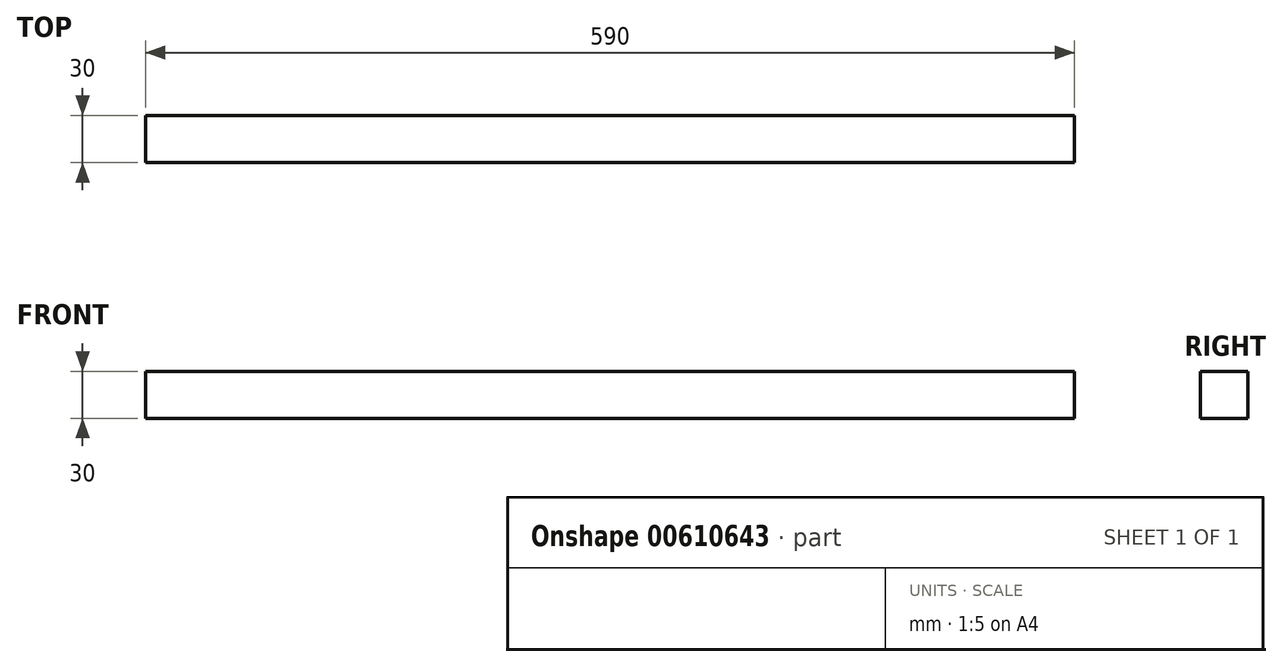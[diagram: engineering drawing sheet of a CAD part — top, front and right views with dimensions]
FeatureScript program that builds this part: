
annotation { "Feature Type Name" : "Feature", "Feature Type Description" : "" }
export const myFeature = defineFeature(function(context is Context, id is Id, definition is map)
    precondition{}
    {
        {
            var Q0;
            Q0=qCreatedBy(makeId("Front.planeOp"),FACE);
            var sketch = newSketch(context, id + "F0", { "sketchPlane" : qUnion([Q0])});
            skLineSegment(sketch, "E0.bottom", {"start": v(-59.04, -188.45) * mm, "end": v(530.96, -188.45) * mm});
            skLineSegment(sketch, "E0.top", {"start": v(-59.04, -218.45) * mm, "end": v(530.96, -218.45) * mm});
            skLineSegment(sketch, "E0.left", {"start": v(-59.04, -188.45) * mm, "end": v(-59.04, -218.45) * mm});
            skLineSegment(sketch, "E0.right", {"start": v(530.96, -188.45) * mm, "end": v(530.96, -218.45) * mm});
            skSolve(sketch);
        }
        {
            var Q0;
            Q0=qSketchRegion(id+"F0",true);
            extrude(context, id + "F1", {"entities" : qUnion([Q0]), "depth" : 30 * mm});
        }
    });
